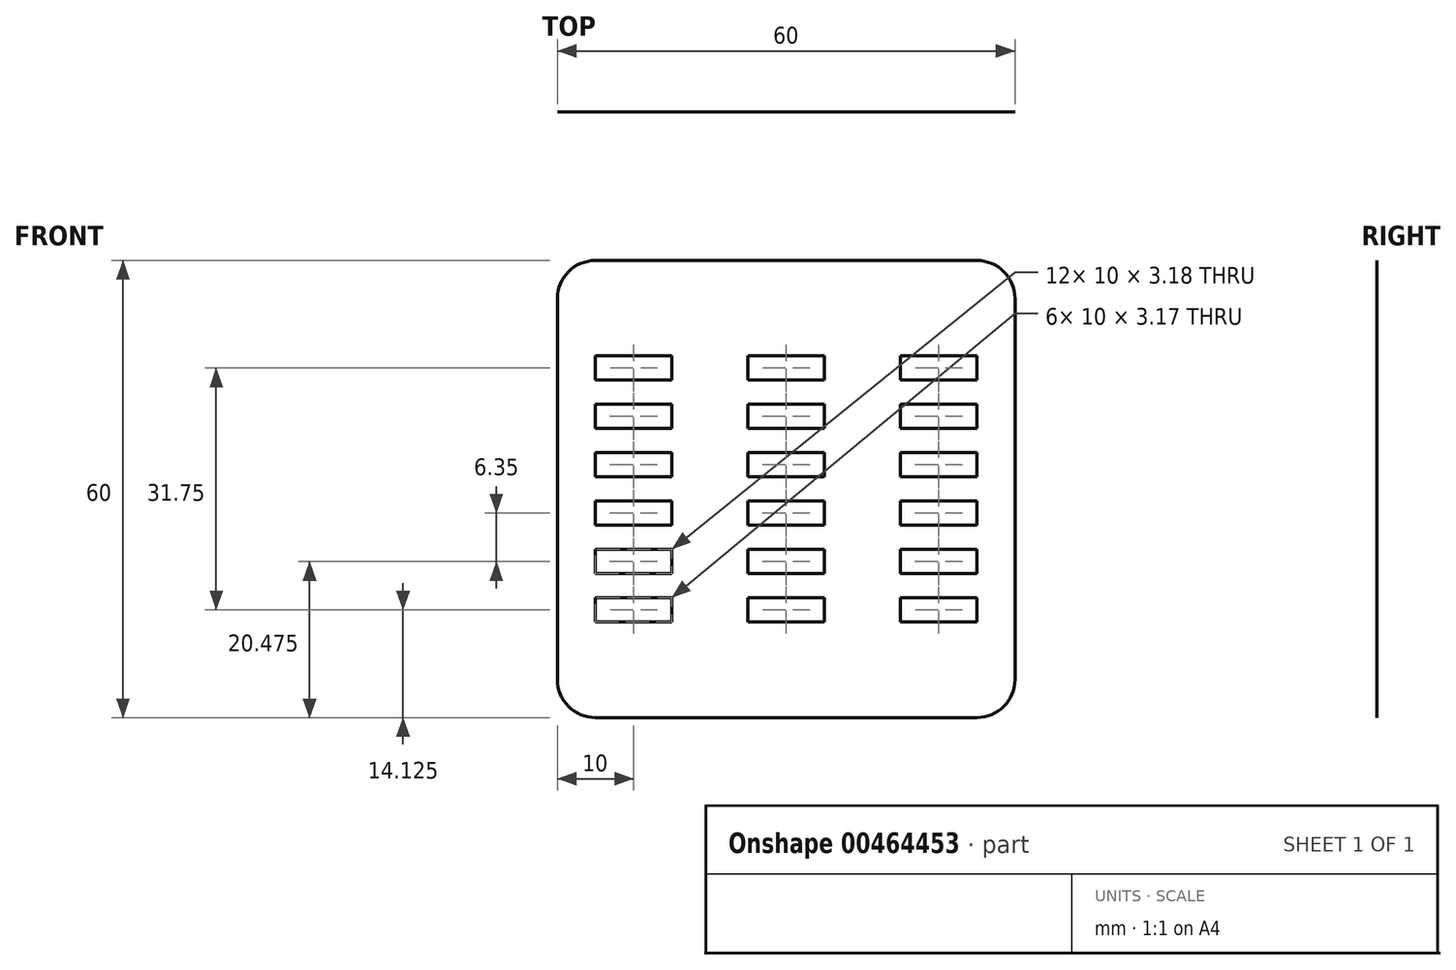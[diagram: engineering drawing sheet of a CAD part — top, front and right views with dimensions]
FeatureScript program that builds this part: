
annotation { "Feature Type Name" : "Feature", "Feature Type Description" : "" }
export const myFeature = defineFeature(function(context is Context, id is Id, definition is map)
    precondition{}
    {
        {
            var Q0;
            Q0=qCreatedBy(makeId("Front.planeOp"),FACE);
            var sketch = newSketch(context, id + "F0", { "sketchPlane" : qUnion([Q0])});
            skLineSegment(sketch, "E0.bottom", {"start": v(-30, 30) * mm, "end": v(30, 30) * mm});
            skLineSegment(sketch, "E0.top", {"start": v(-30, -30) * mm, "end": v(30, -30) * mm});
            skLineSegment(sketch, "E0.left", {"start": v(-30, 30) * mm, "end": v(-30, -30) * mm});
            skLineSegment(sketch, "E0.right", {"start": v(30, 30) * mm, "end": v(30, -30) * mm});
            skSolve(sketch);
        }
        {
            var Q0;
            Q0=makeQuery(id+"F0.imprint","IMPRINT",FACE,{"disambiguationData":[TD([[makeQuery(id+"F0.imprint","IMPRINT",EDGE,{"derivedFrom":sQuery(id+"F0.wireOp",EDGE,"E0.bottom")}),-1.0]])]});
            extrude(context, id + "F1", {"entities" : qUnion([Q0]), "depth" : 1 / 203.2 * mm});
        }
        {
            var Q0;
            Q0=makeQuery(id+"F1.opExtrude","CAP_FACE",FACE,{"disambiguationData":[OSD([sQuery(id+"F0.wireOp",EDGE,"E0.bottom"),sQuery(id+"F0.wireOp",EDGE,"E0.top"),sQuery(id+"F0.wireOp",EDGE,"E0.left"),sQuery(id+"F0.wireOp",EDGE,"E0.right")])],"isStart":false});
            var sketch = newSketch(context, id + "F2", { "sketchPlane" : qUnion([Q0])});
            skLineSegment(sketch, "E1.bottom", {"start": v(-25, -14.29) * mm, "end": v(-15, -14.29) * mm});
            skLineSegment(sketch, "E1.top", {"start": v(-25, -17.46) * mm, "end": v(-15, -17.46) * mm});
            skLineSegment(sketch, "E1.left", {"start": v(-25, -14.29) * mm, "end": v(-25, -17.46) * mm});
            skLineSegment(sketch, "E1.right", {"start": v(-15, -14.29) * mm, "end": v(-15, -17.46) * mm});
            skLineSegment(sketch, "E2.1.0.0", {"start": v(-5, -14.29) * mm, "end": v(5, -14.29) * mm});
            skLineSegment(sketch, "E2.1.0.1", {"start": v(-5, -17.46) * mm, "end": v(5, -17.46) * mm});
            skLineSegment(sketch, "E2.1.0.2", {"start": v(-5, -14.29) * mm, "end": v(-5, -17.46) * mm});
            skLineSegment(sketch, "E2.1.0.3", {"start": v(5, -14.29) * mm, "end": v(5, -17.46) * mm});
            skLineSegment(sketch, "E2.2.0.0", {"start": v(15, -14.29) * mm, "end": v(25, -14.29) * mm});
            skLineSegment(sketch, "E2.2.0.1", {"start": v(15, -17.46) * mm, "end": v(25, -17.46) * mm});
            skLineSegment(sketch, "E2.2.0.2", {"start": v(15, -14.29) * mm, "end": v(15, -17.46) * mm});
            skLineSegment(sketch, "E2.2.0.3", {"start": v(25, -14.29) * mm, "end": v(25, -17.46) * mm});
            skLineSegment(sketch, "E2.direction1", {"start": v(-25, -17.46) * mm, "end": v(-5, -17.46) * mm, "construction": true});
            skLineSegment(sketch, "E3.0.1.0", {"start": v(-25, -7.94) * mm, "end": v(-15, -7.94) * mm});
            skLineSegment(sketch, "E3.0.1.1", {"start": v(-25, -7.94) * mm, "end": v(-25, -11.11) * mm});
            skLineSegment(sketch, "E3.0.1.2", {"start": v(-15, -7.94) * mm, "end": v(-15, -11.11) * mm});
            skLineSegment(sketch, "E3.0.1.3", {"start": v(-5, -7.94) * mm, "end": v(5, -7.94) * mm});
            skLineSegment(sketch, "E3.0.1.4", {"start": v(-5, -11.11) * mm, "end": v(5, -11.11) * mm});
            skLineSegment(sketch, "E3.0.1.5", {"start": v(-5, -7.94) * mm, "end": v(-5, -11.11) * mm});
            skLineSegment(sketch, "E3.0.1.6", {"start": v(-25, -11.11) * mm, "end": v(-5, -11.11) * mm, "construction": true});
            skLineSegment(sketch, "E3.0.1.7", {"start": v(25, -7.94) * mm, "end": v(25, -11.11) * mm});
            skLineSegment(sketch, "E3.0.1.8", {"start": v(15, -7.94) * mm, "end": v(15, -11.11) * mm});
            skLineSegment(sketch, "E3.0.1.9", {"start": v(15, -11.11) * mm, "end": v(25, -11.11) * mm});
            skLineSegment(sketch, "E3.0.1.10", {"start": v(15, -7.94) * mm, "end": v(25, -7.94) * mm});
            skLineSegment(sketch, "E3.0.1.11", {"start": v(5, -7.94) * mm, "end": v(5, -11.11) * mm});
            skLineSegment(sketch, "E3.0.1.12", {"start": v(-25, -11.11) * mm, "end": v(-15, -11.11) * mm});
            skLineSegment(sketch, "E3.0.2.0", {"start": v(-25, -1.59) * mm, "end": v(-15, -1.59) * mm});
            skLineSegment(sketch, "E3.0.2.1", {"start": v(-25, -1.59) * mm, "end": v(-25, -4.76) * mm});
            skLineSegment(sketch, "E3.0.2.2", {"start": v(-15, -1.59) * mm, "end": v(-15, -4.76) * mm});
            skLineSegment(sketch, "E3.0.2.3", {"start": v(-5, -1.59) * mm, "end": v(5, -1.59) * mm});
            skLineSegment(sketch, "E3.0.2.4", {"start": v(-5, -4.76) * mm, "end": v(5, -4.76) * mm});
            skLineSegment(sketch, "E3.0.2.5", {"start": v(-5, -1.59) * mm, "end": v(-5, -4.76) * mm});
            skLineSegment(sketch, "E3.0.2.6", {"start": v(-25, -4.76) * mm, "end": v(-5, -4.76) * mm, "construction": true});
            skLineSegment(sketch, "E3.0.2.7", {"start": v(25, -1.59) * mm, "end": v(25, -4.76) * mm});
            skLineSegment(sketch, "E3.0.2.8", {"start": v(15, -1.59) * mm, "end": v(15, -4.76) * mm});
            skLineSegment(sketch, "E3.0.2.9", {"start": v(15, -4.76) * mm, "end": v(25, -4.76) * mm});
            skLineSegment(sketch, "E3.0.2.10", {"start": v(15, -1.59) * mm, "end": v(25, -1.59) * mm});
            skLineSegment(sketch, "E3.0.2.11", {"start": v(5, -1.59) * mm, "end": v(5, -4.76) * mm});
            skLineSegment(sketch, "E3.0.2.12", {"start": v(-25, -4.76) * mm, "end": v(-15, -4.76) * mm});
            skLineSegment(sketch, "E3.0.3.0", {"start": v(-25, 4.76) * mm, "end": v(-15, 4.76) * mm});
            skLineSegment(sketch, "E3.0.3.1", {"start": v(-25, 4.76) * mm, "end": v(-25, 1.59) * mm});
            skLineSegment(sketch, "E3.0.3.2", {"start": v(-15, 4.76) * mm, "end": v(-15, 1.59) * mm});
            skLineSegment(sketch, "E3.0.3.3", {"start": v(-5, 4.76) * mm, "end": v(5, 4.76) * mm});
            skLineSegment(sketch, "E3.0.3.4", {"start": v(-5, 1.59) * mm, "end": v(5, 1.59) * mm});
            skLineSegment(sketch, "E3.0.3.5", {"start": v(-5, 4.76) * mm, "end": v(-5, 1.59) * mm});
            skLineSegment(sketch, "E3.0.3.6", {"start": v(-25, 1.59) * mm, "end": v(-5, 1.59) * mm, "construction": true});
            skLineSegment(sketch, "E3.0.3.7", {"start": v(25, 4.76) * mm, "end": v(25, 1.59) * mm});
            skLineSegment(sketch, "E3.0.3.8", {"start": v(15, 4.76) * mm, "end": v(15, 1.59) * mm});
            skLineSegment(sketch, "E3.0.3.9", {"start": v(15, 1.59) * mm, "end": v(25, 1.59) * mm});
            skLineSegment(sketch, "E3.0.3.10", {"start": v(15, 4.76) * mm, "end": v(25, 4.76) * mm});
            skLineSegment(sketch, "E3.0.3.11", {"start": v(5, 4.76) * mm, "end": v(5, 1.59) * mm});
            skLineSegment(sketch, "E3.0.3.12", {"start": v(-25, 1.59) * mm, "end": v(-15, 1.59) * mm});
            skLineSegment(sketch, "E3.0.4.0", {"start": v(-25, 11.11) * mm, "end": v(-15, 11.11) * mm});
            skLineSegment(sketch, "E3.0.4.1", {"start": v(-25, 11.11) * mm, "end": v(-25, 7.94) * mm});
            skLineSegment(sketch, "E3.0.4.2", {"start": v(-15, 11.11) * mm, "end": v(-15, 7.94) * mm});
            skLineSegment(sketch, "E3.0.4.3", {"start": v(-5, 11.11) * mm, "end": v(5, 11.11) * mm});
            skLineSegment(sketch, "E3.0.4.4", {"start": v(-5, 7.94) * mm, "end": v(5, 7.94) * mm});
            skLineSegment(sketch, "E3.0.4.5", {"start": v(-5, 11.11) * mm, "end": v(-5, 7.94) * mm});
            skLineSegment(sketch, "E3.0.4.6", {"start": v(-25, 7.94) * mm, "end": v(-5, 7.94) * mm, "construction": true});
            skLineSegment(sketch, "E3.0.4.7", {"start": v(25, 11.11) * mm, "end": v(25, 7.94) * mm});
            skLineSegment(sketch, "E3.0.4.8", {"start": v(15, 11.11) * mm, "end": v(15, 7.94) * mm});
            skLineSegment(sketch, "E3.0.4.9", {"start": v(15, 7.94) * mm, "end": v(25, 7.94) * mm});
            skLineSegment(sketch, "E3.0.4.10", {"start": v(15, 11.11) * mm, "end": v(25, 11.11) * mm});
            skLineSegment(sketch, "E3.0.4.11", {"start": v(5, 11.11) * mm, "end": v(5, 7.94) * mm});
            skLineSegment(sketch, "E3.0.4.12", {"start": v(-25, 7.94) * mm, "end": v(-15, 7.94) * mm});
            skLineSegment(sketch, "E3.direction1", {"start": v(-25, -17.46) * mm, "end": v(0, -17.46) * mm, "construction": true});
            skLineSegment(sketch, "E3.direction2", {"start": v(-25, -17.46) * mm, "end": v(-25, -11.11) * mm, "construction": true});
            skLineSegment(sketch, "E4.0.0.5", {"start": v(-25, 17.46) * mm, "end": v(-15, 17.46) * mm});
            skLineSegment(sketch, "E4.3.0.5", {"start": v(-25, 17.46) * mm, "end": v(-25, 14.29) * mm});
            skLineSegment(sketch, "E4.6.0.5", {"start": v(-15, 17.46) * mm, "end": v(-15, 14.29) * mm});
            skLineSegment(sketch, "E4.9.0.5", {"start": v(-5, 17.46) * mm, "end": v(5, 17.46) * mm});
            skLineSegment(sketch, "E4.12.0.5", {"start": v(-5, 14.29) * mm, "end": v(5, 14.29) * mm});
            skLineSegment(sketch, "E4.15.0.5", {"start": v(-5, 17.46) * mm, "end": v(-5, 14.29) * mm});
            skLineSegment(sketch, "E4.18.0.5", {"start": v(-25, 14.29) * mm, "end": v(-5, 14.29) * mm, "construction": true});
            skLineSegment(sketch, "E4.21.0.5", {"start": v(25, 17.46) * mm, "end": v(25, 14.29) * mm});
            skLineSegment(sketch, "E4.24.0.5", {"start": v(15, 17.46) * mm, "end": v(15, 14.29) * mm});
            skLineSegment(sketch, "E4.27.0.5", {"start": v(15, 14.29) * mm, "end": v(25, 14.29) * mm});
            skLineSegment(sketch, "E4.30.0.5", {"start": v(15, 17.46) * mm, "end": v(25, 17.46) * mm});
            skLineSegment(sketch, "E4.33.0.5", {"start": v(5, 17.46) * mm, "end": v(5, 14.29) * mm});
            skLineSegment(sketch, "E4.36.0.5", {"start": v(-25, 14.29) * mm, "end": v(-15, 14.29) * mm});
            skSolve(sketch);
        }
        {
            var Q0;
            Q0 = qSketchRegion(id + "F2", true);
            extrude(context, id + "F3", {"entities" : qUnion([Q0]), "operationType" : NewBodyOperationType.REMOVE, "endBound" : BoundingType.THROUGH_ALL, "oppositeDirection" : true, "depth" : 25 * mm});
        }
        {
            var Q0;
            Q0=makeQuery(id+"F1.opExtrude","SWEPT_EDGE",EDGE,{"disambiguationData":[OSD([sQuery(id+"F0.wireOp",EDGE,"E0.bottom"),sQuery(id+"F0.wireOp",EDGE,"E0.left")])]});
            var Q1;
            Q1=makeQuery(id+"F1.opExtrude","SWEPT_EDGE",EDGE,{"disambiguationData":[OSD([sQuery(id+"F0.wireOp",EDGE,"E0.bottom"),sQuery(id+"F0.wireOp",EDGE,"E0.right")])]});
            var Q2;
            Q2=makeQuery(id+"F1.opExtrude","SWEPT_EDGE",EDGE,{"disambiguationData":[OSD([sQuery(id+"F0.wireOp",EDGE,"E0.top"),sQuery(id+"F0.wireOp",EDGE,"E0.left")])]});
            var Q3;
            Q3=makeQuery(id+"F1.opExtrude","SWEPT_EDGE",EDGE,{"disambiguationData":[OSD([sQuery(id+"F0.wireOp",EDGE,"E0.top"),sQuery(id+"F0.wireOp",EDGE,"E0.right")])]});
            fillet(context, id + "F4", {"entities" : qUnion([Q0, Q1, Q2, Q3]), "radius" : 5 * mm, "tangentPropagation" : true, "allowEdgeOverflow" : false});
        }
    });
